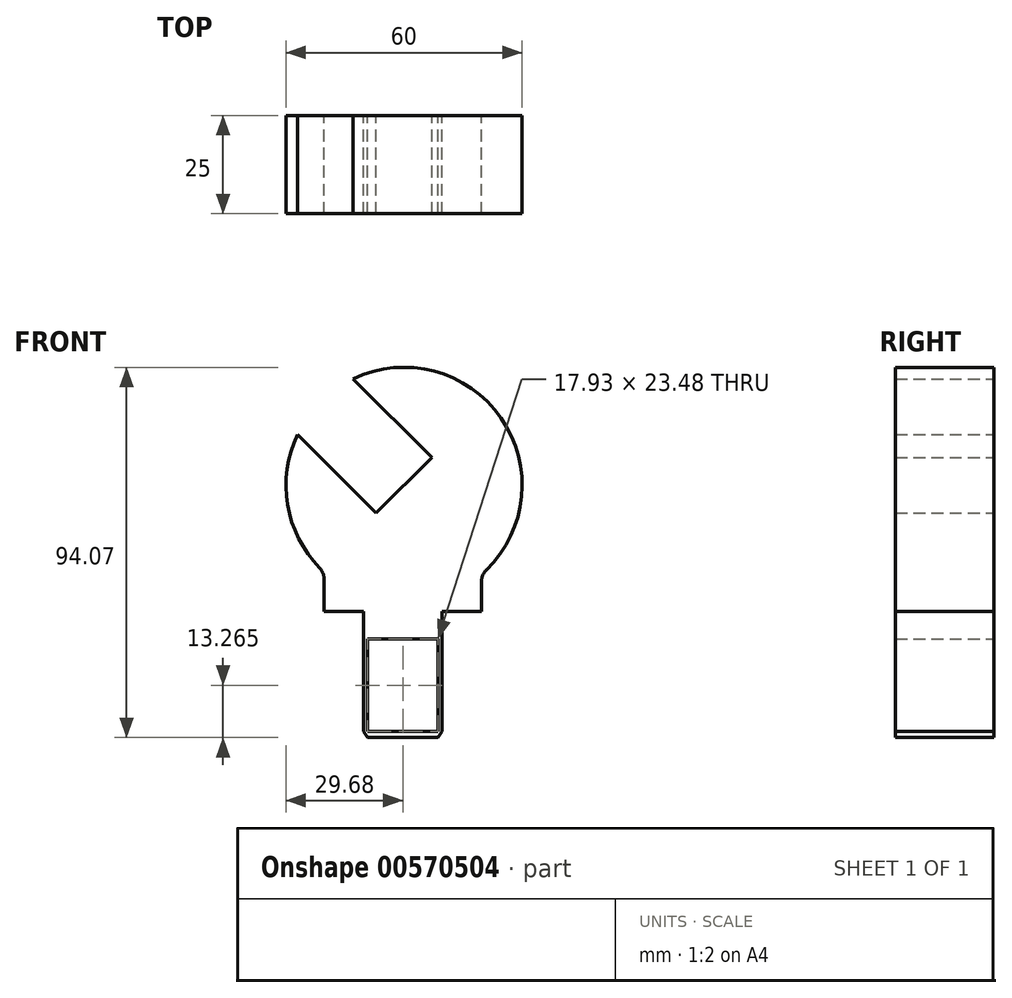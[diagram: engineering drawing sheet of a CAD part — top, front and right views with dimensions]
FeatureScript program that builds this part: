
annotation { "Feature Type Name" : "Feature", "Feature Type Description" : "" }
export const myFeature = defineFeature(function(context is Context, id is Id, definition is map)
    precondition{}
    {
        {
            var Q0;
            Q0=qCreatedBy(makeId("Front.planeOp"),FACE);
            var sketch = newSketch(context, id + "F0", { "sketchPlane" : qUnion([Q0])});
            skLineSegment(sketch, "E0", {"start": v(-32.16, 22) * mm, "end": v(33.18, 22) * mm, "construction": true});
            skLineSegment(sketch, "E1", {"start": v(0, 63.36) * mm, "end": v(0, -48.68) * mm, "construction": true});
            skArc(sketch, "E2", {"start": v(-26.75, 34.93) * mm, "mid": v(-29.27, 17.1) * mm, "end": v(-21.14, 1.04) * mm});
            skLineSegment(sketch, "E3", {"start": v(0.32, 22) * mm, "end": v(7.4, 29.07) * mm});
            skLineSegment(sketch, "E4", {"start": v(0.32, 22) * mm, "end": v(-6.75, 14.93) * mm});
            skLineSegment(sketch, "E5", {"start": v(-6.75, 14.93) * mm, "end": v(-26.75, 34.93) * mm});
            skLineSegment(sketch, "E6", {"start": v(7.4, 29.07) * mm, "end": v(-12.6, 49.07) * mm});
            skLineSegment(sketch, "E7", {"start": v(0, -10.07) * mm, "end": v(-20, -10.07) * mm});
            skLineSegment(sketch, "E8", {"start": v(-20, -10.07) * mm, "end": v(-20, -1.76) * mm});
            skLineSegment(sketch, "E9.MirrorCS", {"start": v(0, -10.07) * mm, "end": v(20, -10.07) * mm});
            skLineSegment(sketch, "E10.MirrorCS", {"start": v(20, -10.07) * mm, "end": v(20, -2.4) * mm});
            skArc(sketch, "E11.trimOffspring", {"start": v(21.21, 0.47) * mm, "mid": v(24.95, 39.13) * mm, "end": v(-12.6, 49.07) * mm});
            skPoint(sketch, "E12.visualSharp", {"position": v(-20, -0.07) * mm});
            skArc(sketch, "E12.filletArc", {"start": v(-20, -1.76) * mm, "mid": v(-20.3, -0.25) * mm, "end": v(-21.14, 1.04) * mm});
            skPoint(sketch, "E13.newPointB", {"position": v(20, -0.07) * mm});
            skArc(sketch, "E13.filletArc", {"start": v(21.21, 0.47) * mm, "mid": v(20.32, -0.84) * mm, "end": v(20, -2.4) * mm});
            skLineSegment(sketch, "E14", {"start": v(-10, -10.07) * mm, "end": v(-10, -40.54) * mm});
            skLineSegment(sketch, "E15", {"start": v(-10, -17.07) * mm, "end": v(0, -17.07) * mm});
            skLineSegment(sketch, "E16.MirrorCS", {"start": v(10, -17.07) * mm, "end": v(0, -17.07) * mm});
            skLineSegment(sketch, "E17.MirrorCS", {"start": v(10, -10.07) * mm, "end": v(10, -40.54) * mm});
            skLineSegment(sketch, "E18", {"start": v(-8.96, -42.07) * mm, "end": v(8.96, -42.07) * mm});
            skLineSegment(sketch, "E19", {"start": v(-8.96, -17.07) * mm, "end": v(-8.96, -42.07) * mm});
            skLineSegment(sketch, "E20", {"start": v(-10, -40.54) * mm, "end": v(0, -40.54) * mm});
            skLineSegment(sketch, "E21.MirrorCS", {"start": v(10, -40.54) * mm, "end": v(0, -40.54) * mm});
            skLineSegment(sketch, "E22.MirrorCS", {"start": v(8.96, -17.07) * mm, "end": v(8.96, -42.07) * mm});
            skLineSegment(sketch, "E23", {"start": v(-10, -40.54) * mm, "end": v(-8.96, -42.07) * mm});
            skLineSegment(sketch, "E24", {"start": v(10, -40.54) * mm, "end": v(8.96, -42.07) * mm});
            skPoint(sketch, "E25.orphan", {"position": v(-10, -42.07) * mm});
            skPoint(sketch, "E26.orphan", {"position": v(10, -42.07) * mm});
            skSolve(sketch);
        }
        {
            var Q0;
            Q0 = qSketchRegion(id + "F0", true);
            extrude(context, id + "F1", {"entities" : qUnion([Q0]), "depth" : 25 * mm, "offsetDistance" : 25 * mm});
        }
    });
